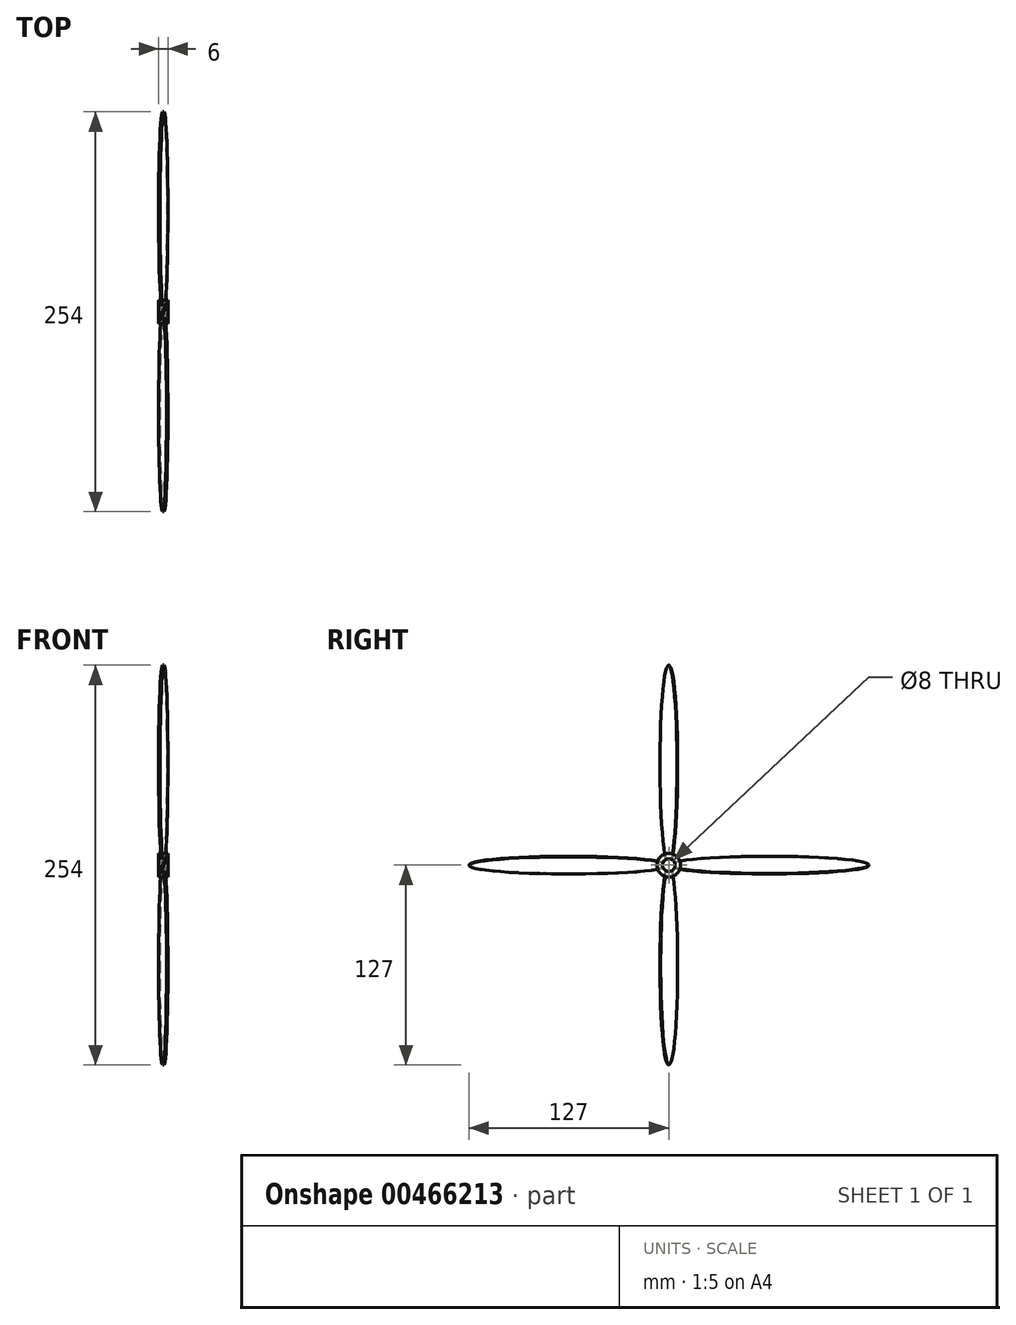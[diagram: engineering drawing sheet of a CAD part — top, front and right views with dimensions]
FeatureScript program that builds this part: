
annotation { "Feature Type Name" : "Feature", "Feature Type Description" : "" }
export const myFeature = defineFeature(function(context is Context, id is Id, definition is map)
    precondition{}
    {
        {
            var Q0;
            Q0=qCreatedBy(makeId("Front.planeOp"),FACE);
            var sketch = newSketch(context, id + "F0", { "sketchPlane" : qUnion([Q0])});
            skLineSegment(sketch, "E0", {"start": v(24.05, 51.58) * mm, "end": v(-16.88, -36.2) * mm, "construction": true});
            skSolve(sketch);
        }
        {
            var Q0;
            Q0=sQuery(id+"F0.wireOp",EDGE,"E0");
            cPlane(context, id + "F1", {"entities" : qUnion([Q0]), "cplaneType" : CPlaneType.LINE_ANGLE, "offset" : 25 * mm, "angle" : 0 * degree, "width" : 150 * mm, "height" : 150 * mm});
        }
        {
            var Q0;
            Q0=qCreatedBy(id+"F1.planeOp",FACE);
            var sketch = newSketch(context, id + "F2", { "sketchPlane" : qUnion([Q0])});
            skEllipse(sketch, "E1", {"center": v(63.5, 0) * mm, "majorRadius": 63.5 * mm, "minorRadius": 6 * mm, "majorAxis": v(1, 0)});
            skSolve(sketch);
        }
        {
            var Q0;
            Q0=makeQuery(id+"F2.imprint","IMPRINT",FACE,{"disambiguationData":[TD([[makeQuery(id+"F2.imprint","IMPRINT",EDGE,{"derivedFrom":sQuery(id+"F2.wireOp",EDGE,"E1")}),1.0]])]});
            extrude(context, id + "F3", {"entities" : qUnion([Q0]), "endBound" : BoundingType.SYMMETRIC, "depth" : 1 * mm});
        }
        {
            var Q0;
            Q0=qCreatedBy(makeId("Front.planeOp"),FACE);
            var sketch = newSketch(context, id + "F4", { "sketchPlane" : qUnion([Q0])});
            skLineSegment(sketch, "E2", {"start": v(-40.3, 0) * mm, "end": v(42.6, 0) * mm, "construction": true});
            skSolve(sketch);
        }
        {
            var Q0;
            Q0=qCreatedBy(makeId("Right.planeOp"),FACE);
            var sketch = newSketch(context, id + "F5", { "sketchPlane" : qUnion([Q0])});
            skCircle(sketch, "E3", {"center": v(0, 0) * mm, "radius": 7.5 * mm});
            skCircle(sketch, "E4", {"center": v(0, 0) * mm, "radius": 4 * mm});
            skSolve(sketch);
        }
        {
            var Q0;
            Q0=makeQuery(id+"F5.imprint","IMPRINT",FACE,{"disambiguationData":[TD([[makeQuery(id+"F5.imprint","IMPRINT",EDGE,{"derivedFrom":sQuery(id+"F5.wireOp",EDGE,"E4")}),1.0]])]});
            var Q1;
            Q1=sQuery(id+"F5.wireOp",EDGE,"E4");
            extrude(context, id + "F6", {"entities" : qUnion([Q0]), "surfaceEntities" : qUnion([Q1]), "endBound" : BoundingType.SYMMETRIC, "depth" : 50 * mm});
        }
        {
            var Q0;
            Q0=makeQuery(id+"F6.opExtrude","SWEPT_BODY",BODY,{"disambiguationData":[OSD([sQuery(id+"F5.wireOp",EDGE,"E4")])]});
            var Q1;
            Q1=makeQuery(id+"F9.opPattern","COPY",BODY,{"derivedFrom":makeQuery(id+"F3.opExtrude","SWEPT_BODY",BODY,{"disambiguationData":[OSD([sQuery(id+"F2.wireOp",EDGE,"E1"),sQuery(id+"F2.wireOp",EDGE,"T1zounnW-mgMH-tI4i-LY2v-MLyvGf9OsOFz")])]}),"instanceName":"1"});
            var Q2;
            Q2=makeQuery(id+"F9.opPattern","COPY",BODY,{"derivedFrom":makeQuery(id+"F3.opExtrude","SWEPT_BODY",BODY,{"disambiguationData":[OSD([sQuery(id+"F2.wireOp",EDGE,"E1"),sQuery(id+"F2.wireOp",EDGE,"T1zounnW-mgMH-tI4i-LY2v-MLyvGf9OsOFz")])]}),"instanceName":"2"});
            var Q3;
            Q3=makeQuery(id+"F3.opExtrude","SWEPT_BODY",BODY,{"disambiguationData":[OSD([sQuery(id+"F2.wireOp",EDGE,"E1"),sQuery(id+"F2.wireOp",EDGE,"T1zounnW-mgMH-tI4i-LY2v-MLyvGf9OsOFz")])]});
            booleanBodies(context, id + "F7", {"operationType" : BooleanOperationType.SUBTRACTION, "tools" : qUnion([Q0]), "targets" : qUnion([Q1, Q2, Q3])});
        }
        {
            var Q0;
            Q0=makeQuery(id+"F5.imprint","IMPRINT",FACE,{"disambiguationData":[TD([[makeQuery(id+"F5.imprint","IMPRINT",EDGE,{"derivedFrom":sQuery(id+"F5.wireOp",EDGE,"E3")}),1.0]])]});
            extrude(context, id + "F8", {"entities" : qUnion([Q0]), "endBound" : BoundingType.SYMMETRIC, "depth" : 6 * mm});
        }
        {
            var Q0;
            Q0=makeQuery(id+"F3.opExtrude","SWEPT_BODY",BODY,{"disambiguationData":[OSD([sQuery(id+"F2.wireOp",EDGE,"E1"),sQuery(id+"F2.wireOp",EDGE,"T1zounnW-mgMH-tI4i-LY2v-MLyvGf9OsOFz")])]});
            var Q1;
            Q1=sQuery(id+"F4.wireOp",EDGE,"E2");
            circularPattern(context, id + "F9", {"entities" : qUnion([Q0]), "axis" : qUnion([Q1]), "angle" : 360 * degree, "instanceCount" : 4, "equalSpace" : true});
        }
    });
